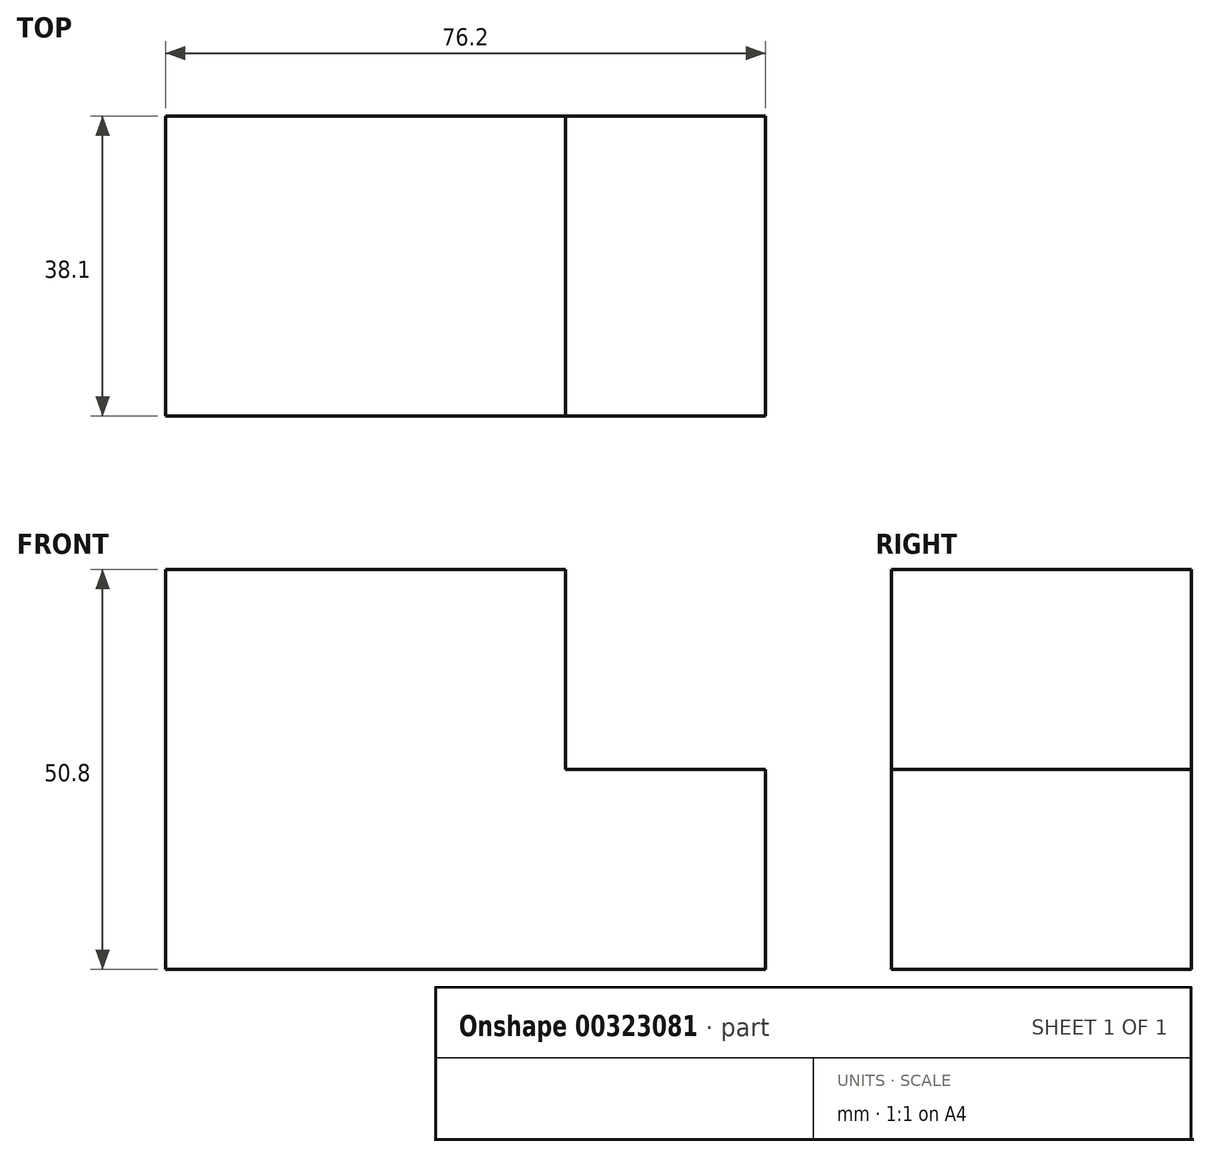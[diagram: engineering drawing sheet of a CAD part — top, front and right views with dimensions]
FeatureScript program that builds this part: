
annotation { "Feature Type Name" : "Feature", "Feature Type Description" : "" }
export const myFeature = defineFeature(function(context is Context, id is Id, definition is map)
    precondition{}
    {
        {
            var Q0;
            Q0=qCreatedBy(makeId("Front.planeOp"),FACE);
            var sketch = newSketch(context, id + "F0", { "sketchPlane" : qUnion([Q0])});
            skLineSegment(sketch, "E0", {"start": v(-41.11, -32.34) * mm, "end": v(35.09, -32.34) * mm});
            skLineSegment(sketch, "E1", {"start": v(-41.11, -32.34) * mm, "end": v(-41.11, 18.46) * mm});
            skLineSegment(sketch, "E2", {"start": v(-41.11, 18.46) * mm, "end": v(9.69, 18.46) * mm});
            skLineSegment(sketch, "E3", {"start": v(9.69, 18.46) * mm, "end": v(9.69, -6.94) * mm});
            skLineSegment(sketch, "E4", {"start": v(9.69, -6.94) * mm, "end": v(35.09, -6.94) * mm});
            skLineSegment(sketch, "E5", {"start": v(35.09, -6.94) * mm, "end": v(35.09, -32.34) * mm});
            skSolve(sketch);
        }
        {
            var Q0;
            Q0=makeQuery(id+"F0.imprint","IMPRINT",FACE,{"disambiguationData":[TD([[makeQuery(id+"F0.imprint","IMPRINT",EDGE,{"derivedFrom":sQuery(id+"F0.wireOp",EDGE,"E0")}),1.0]])]});
            extrude(context, id + "F1", {"entities" : qUnion([Q0]), "depth" : 38.1 * mm});
        }
    });
